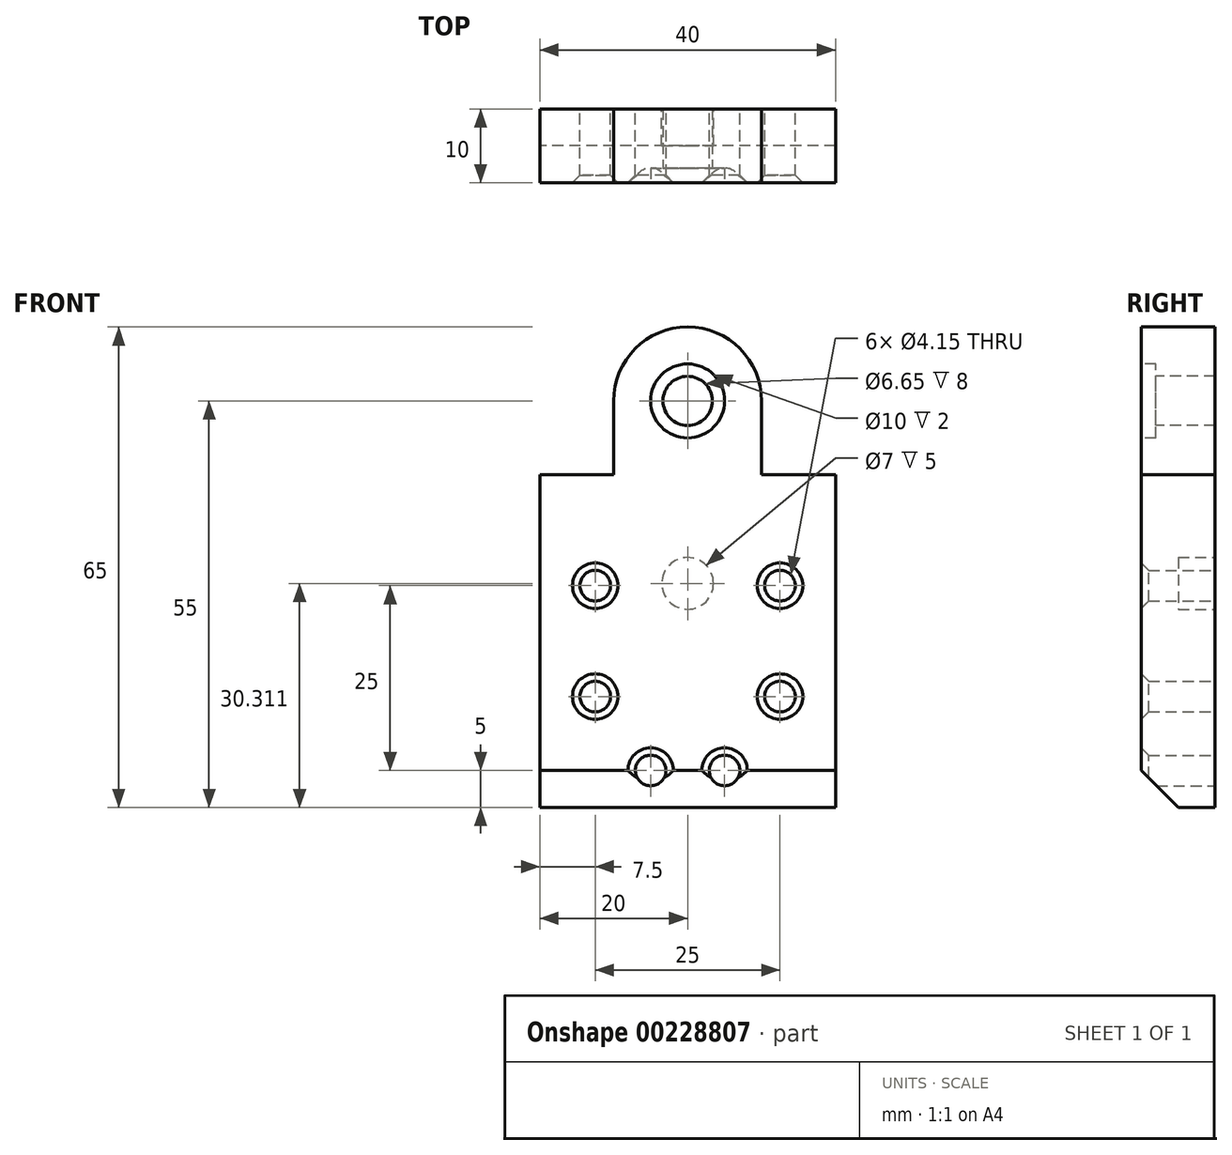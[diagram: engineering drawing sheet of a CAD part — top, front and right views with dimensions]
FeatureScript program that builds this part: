
annotation { "Feature Type Name" : "Feature", "Feature Type Description" : "" }
export const myFeature = defineFeature(function(context is Context, id is Id, definition is map)
    precondition{}
    {
        {
            var Q0;
            Q0=qCreatedBy(makeId("Front.planeOp"),FACE);
            var sketch = newSketch(context, id + "F0", { "sketchPlane" : qUnion([Q0])});
            skLineSegment(sketch, "E0.bottom", {"start": v(-20, 20) * mm, "end": v(20, 20) * mm});
            skLineSegment(sketch, "E0.top", {"start": v(-20, -20) * mm, "end": v(20, -20) * mm});
            skLineSegment(sketch, "E0.left", {"start": v(-20, 20) * mm, "end": v(-20, -20) * mm});
            skLineSegment(sketch, "E0.right", {"start": v(20, 20) * mm, "end": v(20, -20) * mm});
            skCircle(sketch, "E1", {"center": v(-5, -15) * mm, "radius": 2.07 * mm});
            skCircle(sketch, "E2.MirrorC", {"center": v(5, -15) * mm, "radius": 2.07 * mm});
            skCircle(sketch, "E3", {"center": v(-12.5, 10) * mm, "radius": 2.07 * mm});
            skCircle(sketch, "E4.MirrorC", {"center": v(12.5, 10) * mm, "radius": 2.07 * mm});
            skLineSegment(sketch, "E5", {"start": v(-20, 2.5) * mm, "end": v(0, 2.5) * mm, "construction": true});
            skCircle(sketch, "E6.MirrorC", {"center": v(-12.5, -5) * mm, "radius": 2.07 * mm});
            skCircle(sketch, "E7.MirrorC", {"center": v(12.5, -5) * mm, "radius": 2.07 * mm});
            skSolve(sketch);
        }
        {
            var Q0;
            Q0=makeQuery(id+"F0.imprint","IMPRINT",FACE,{"disambiguationData":[TD([[makeQuery(id+"F0.imprint","IMPRINT",EDGE,{"derivedFrom":sQuery(id+"F0.wireOp",EDGE,"E0.bottom")}),-1.0]])]});
            extrude(context, id + "F1", {"entities" : qUnion([Q0]), "depth" : 10 * mm});
        }
        {
            var Q0;
            Q0=makeQuery(id+"F1.opExtrude","CAP_FACE",FACE,{"disambiguationData":[OSD([sQuery(id+"F0.wireOp",EDGE,"E0.bottom"),sQuery(id+"F0.wireOp",EDGE,"E0.top"),sQuery(id+"F0.wireOp",EDGE,"E0.left"),sQuery(id+"F0.wireOp",EDGE,"E0.right"),sQuery(id+"F0.wireOp",EDGE,"E1"),sQuery(id+"F0.wireOp",EDGE,"E2.MirrorC"),sQuery(id+"F0.wireOp",EDGE,"E3"),sQuery(id+"F0.wireOp",EDGE,"E4.MirrorC")])],"isStart":false});
            var sketch = newSketch(context, id + "F2", { "sketchPlane" : qUnion([Q0])});
            skArc(sketch, "E8", {"start": v(10, 35) * mm, "mid": v(0, 45) * mm, "end": v(-10, 35) * mm});
            skLineSegment(sketch, "E9", {"start": v(-10, 35) * mm, "end": v(-10, 20) * mm});
            skLineSegment(sketch, "E10", {"start": v(10, 35) * mm, "end": v(10, 20) * mm});
            skLineSegment(sketch, "E11.bottom", {"start": v(-20, 25) * mm, "end": v(-10, 25) * mm});
            skLineSegment(sketch, "E11.top", {"start": v(-20, 20) * mm, "end": v(-10, 20) * mm});
            skLineSegment(sketch, "E11.left", {"start": v(-20, 25) * mm, "end": v(-20, 20) * mm});
            skLineSegment(sketch, "E11.right", {"start": v(-10, 25) * mm, "end": v(-10, 20) * mm});
            skLineSegment(sketch, "E12.bottom", {"start": v(20, 25) * mm, "end": v(10, 25) * mm});
            skLineSegment(sketch, "E12.top", {"start": v(20, 20) * mm, "end": v(10, 20) * mm});
            skLineSegment(sketch, "E12.left", {"start": v(20, 25) * mm, "end": v(20, 20) * mm});
            skLineSegment(sketch, "E12.right", {"start": v(10, 25) * mm, "end": v(10, 20) * mm});
            skSolve(sketch);
        }
        {
            var Q0;
            Q0=makeQuery(id+"F2.imprint","IMPRINT",FACE,{"disambiguationData":[TD([[makeQuery(id+"F2.imprint","IMPRINT",EDGE,{"derivedFrom":sQuery(id+"F2.wireOp",EDGE,"E8")}),1.0]])]});
            var Q1;
            Q1=makeQuery(id+"F2.imprint","IMPRINT",FACE,{"disambiguationData":[TD([[makeQuery(id+"F2.imprint","IMPRINT",EDGE,{"derivedFrom":sQuery(id+"F2.wireOp",EDGE,"E11.bottom")}),-1.0]])]});
            var Q2;
            Q2=makeQuery(id+"F2.imprint","IMPRINT",FACE,{"disambiguationData":[TD([[makeQuery(id+"F2.imprint","IMPRINT",EDGE,{"derivedFrom":sQuery(id+"F2.wireOp",EDGE,"E12.bottom")}),1.0]])]});
            var Q3;
            Q3=makeQuery(id+"F1.opExtrude","CAP_FACE",FACE,{"disambiguationData":[OSD([sQuery(id+"F0.wireOp",EDGE,"E0.bottom"),sQuery(id+"F0.wireOp",EDGE,"E0.top"),sQuery(id+"F0.wireOp",EDGE,"E0.left"),sQuery(id+"F0.wireOp",EDGE,"E0.right"),sQuery(id+"F0.wireOp",EDGE,"E1"),sQuery(id+"F0.wireOp",EDGE,"E2.MirrorC"),sQuery(id+"F0.wireOp",EDGE,"E3"),sQuery(id+"F0.wireOp",EDGE,"E4.MirrorC")])],"isStart":true});
            extrude(context, id + "F3", {"entities" : qUnion([Q0, Q1, Q2]), "operationType" : NewBodyOperationType.ADD, "endBound" : BoundingType.UP_TO_SURFACE, "oppositeDirection" : true, "endBoundEntityFace" : qUnion([Q3]), "depth" : 25 * mm});
        }
        {
            var Q0;
            Q0=makeQuery(id+"F1.opExtrude","CAP_EDGE",EDGE,{"disambiguationData":[OSD([sQuery(id+"F0.wireOp",EDGE,"E1")])],"isStart":false});
            var Q1;
            Q1=makeQuery(id+"F1.opExtrude","CAP_EDGE",EDGE,{"disambiguationData":[OSD([sQuery(id+"F0.wireOp",EDGE,"E2.MirrorC")])],"isStart":false});
            var Q2;
            Q2=makeQuery(id+"F1.opExtrude","CAP_EDGE",EDGE,{"disambiguationData":[OSD([sQuery(id+"F0.wireOp",EDGE,"E3")])],"isStart":false});
            var Q3;
            Q3=makeQuery(id+"F1.opExtrude","CAP_EDGE",EDGE,{"disambiguationData":[OSD([sQuery(id+"F0.wireOp",EDGE,"E6.MirrorC")])],"isStart":false});
            var Q4;
            Q4=makeQuery(id+"F1.opExtrude","CAP_EDGE",EDGE,{"disambiguationData":[OSD([sQuery(id+"F0.wireOp",EDGE,"E7.MirrorC")])],"isStart":false});
            var Q5;
            Q5=makeQuery(id+"F1.opExtrude","CAP_EDGE",EDGE,{"disambiguationData":[OSD([sQuery(id+"F0.wireOp",EDGE,"E4.MirrorC")])],"isStart":false});
            chamfer(context, id + "F4", {"entities" : qUnion([Q0, Q1, Q2, Q3, Q4, Q5]), "width" : 1 * mm, "tangentPropagation" : true});
        }
        {
            var Q0;
            {var subQ0=sQuery(id+"F0.wireOp",EDGE,"E0.bottom");Q0=makeQuery(id+"F3.boolean.opBoolean","MERGE",FACE,{"derivedFrom":[makeQuery(id+"F1.opExtrude","CAP_FACE",FACE,{"disambiguationData":[OSD([subQ0,sQuery(id+"F0.wireOp",EDGE,"E0.top"),sQuery(id+"F0.wireOp",EDGE,"E0.left"),sQuery(id+"F0.wireOp",EDGE,"E0.right"),sQuery(id+"F0.wireOp",EDGE,"E1"),sQuery(id+"F0.wireOp",EDGE,"E2.MirrorC"),sQuery(id+"F0.wireOp",EDGE,"E3"),sQuery(id+"F0.wireOp",EDGE,"E4.MirrorC"),sQuery(id+"F0.wireOp",EDGE,"E6.MirrorC"),sQuery(id+"F0.wireOp",EDGE,"E7.MirrorC")])],"isStart":false}),makeQuery(id+"F3.opExtrude","CAP_FACE",FACE,{"disambiguationData":[OSD([subQ0,sQuery(id+"F2.wireOp",EDGE,"E8"),sQuery(id+"F2.wireOp",EDGE,"E9"),sQuery(id+"F2.wireOp",EDGE,"E10"),sQuery(id+"F2.wireOp",EDGE,"E11.bottom"),sQuery(id+"F2.wireOp",EDGE,"E11.top"),sQuery(id+"F2.wireOp",EDGE,"E11.left"),sQuery(id+"F2.wireOp",EDGE,"E12.bottom"),sQuery(id+"F2.wireOp",EDGE,"E12.top"),sQuery(id+"F2.wireOp",EDGE,"E12.left")])],"isStart":true})]});}
            var sketch = newSketch(context, id + "F5", { "sketchPlane" : qUnion([Q0])});
            skCircle(sketch, "E13", {"center": v(0, 35) * mm, "radius": 3.32 * mm});
            skSolve(sketch);
        }
        {
            var Q0;
            Q0=makeQuery(id+"F5.imprint","IMPRINT",FACE,{"disambiguationData":[TD([[makeQuery(id+"F5.imprint","IMPRINT",EDGE,{"derivedFrom":sQuery(id+"F5.wireOp",EDGE,"E13")}),1.0]])]});
            extrude(context, id + "F6", {"entities" : qUnion([Q0]), "operationType" : NewBodyOperationType.REMOVE, "endBound" : BoundingType.THROUGH_ALL, "oppositeDirection" : true, "depth" : 25 * mm});
        }
        {
            var Q0;
            {var subQ0=sQuery(id+"F0.wireOp",EDGE,"E0.bottom");Q0=makeQuery(id+"F3.boolean.opBoolean","MERGE",FACE,{"derivedFrom":[makeQuery(id+"F1.opExtrude","CAP_FACE",FACE,{"disambiguationData":[OSD([subQ0,sQuery(id+"F0.wireOp",EDGE,"E0.top"),sQuery(id+"F0.wireOp",EDGE,"E0.left"),sQuery(id+"F0.wireOp",EDGE,"E0.right"),sQuery(id+"F0.wireOp",EDGE,"E1"),sQuery(id+"F0.wireOp",EDGE,"E2.MirrorC"),sQuery(id+"F0.wireOp",EDGE,"E3"),sQuery(id+"F0.wireOp",EDGE,"E4.MirrorC"),sQuery(id+"F0.wireOp",EDGE,"E6.MirrorC"),sQuery(id+"F0.wireOp",EDGE,"E7.MirrorC")])],"isStart":false}),makeQuery(id+"F3.opExtrude","CAP_FACE",FACE,{"disambiguationData":[OSD([subQ0,sQuery(id+"F2.wireOp",EDGE,"E8"),sQuery(id+"F2.wireOp",EDGE,"E9"),sQuery(id+"F2.wireOp",EDGE,"E10"),sQuery(id+"F2.wireOp",EDGE,"E11.bottom"),sQuery(id+"F2.wireOp",EDGE,"E11.top"),sQuery(id+"F2.wireOp",EDGE,"E11.left"),sQuery(id+"F2.wireOp",EDGE,"E12.bottom"),sQuery(id+"F2.wireOp",EDGE,"E12.top"),sQuery(id+"F2.wireOp",EDGE,"E12.left")])],"isStart":true})]});}
            var sketch = newSketch(context, id + "F7", { "sketchPlane" : qUnion([Q0])});
            skCircle(sketch, "E14", {"center": v(0, 35) * mm, "radius": 5 * mm});
            skSolve(sketch);
        }
        {
            var Q0;
            Q0=makeQuery(id+"F7.imprint","IMPRINT",FACE,{"disambiguationData":[TD([[makeQuery(id+"F7.imprint","IMPRINT",EDGE,{"derivedFrom":sQuery(id+"F7.wireOp",EDGE,"E14")}),1.0]])]});
            extrude(context, id + "F8", {"entities" : qUnion([Q0]), "operationType" : NewBodyOperationType.REMOVE, "oppositeDirection" : true, "depth" : 2 * mm});
        }
        {
            var Q0;
            {var subQ0=sQuery(id+"F0.wireOp",EDGE,"E0.bottom");Q0=makeQuery(id+"F3.boolean.opBoolean","MERGE",FACE,{"derivedFrom":[makeQuery(id+"F1.opExtrude","CAP_FACE",FACE,{"disambiguationData":[OSD([subQ0,sQuery(id+"F0.wireOp",EDGE,"E0.top"),sQuery(id+"F0.wireOp",EDGE,"E0.left"),sQuery(id+"F0.wireOp",EDGE,"E0.right"),sQuery(id+"F0.wireOp",EDGE,"E1"),sQuery(id+"F0.wireOp",EDGE,"E2.MirrorC"),sQuery(id+"F0.wireOp",EDGE,"E3"),sQuery(id+"F0.wireOp",EDGE,"E4.MirrorC"),sQuery(id+"F0.wireOp",EDGE,"E6.MirrorC"),sQuery(id+"F0.wireOp",EDGE,"E7.MirrorC")])],"isStart":false}),makeQuery(id+"F3.opExtrude","CAP_FACE",FACE,{"disambiguationData":[OSD([subQ0,sQuery(id+"F2.wireOp",EDGE,"E8"),sQuery(id+"F2.wireOp",EDGE,"E9"),sQuery(id+"F2.wireOp",EDGE,"E10"),sQuery(id+"F2.wireOp",EDGE,"E11.bottom"),sQuery(id+"F2.wireOp",EDGE,"E11.top"),sQuery(id+"F2.wireOp",EDGE,"E11.left"),sQuery(id+"F2.wireOp",EDGE,"E12.bottom"),sQuery(id+"F2.wireOp",EDGE,"E12.top"),sQuery(id+"F2.wireOp",EDGE,"E12.left")])],"isStart":true})]});}
            var Q1;
            {var subQ0=sQuery(id+"F0.wireOp",EDGE,"E7.MirrorC");var subQ1=sQuery(id+"F0.wireOp",EDGE,"E6.MirrorC");var subQ2=sQuery(id+"F0.wireOp",EDGE,"E4.MirrorC");var subQ3=sQuery(id+"F0.wireOp",EDGE,"E3");var subQ4=sQuery(id+"F0.wireOp",EDGE,"E2.MirrorC");var subQ5=sQuery(id+"F0.wireOp",EDGE,"E1");var subQ6=sQuery(id+"F0.wireOp",EDGE,"E0.right");var subQ7=sQuery(id+"F0.wireOp",EDGE,"E0.left");var subQ8=sQuery(id+"F0.wireOp",EDGE,"E0.top");var subQ9=sQuery(id+"F0.wireOp",EDGE,"E0.bottom");Q1=makeQuery(id+"F3.boolean.opBoolean","MERGE",FACE,{"derivedFrom":[makeQuery(id+"F1.opExtrude","CAP_FACE",FACE,{"disambiguationData":[OSD([subQ9,subQ8,subQ7,subQ6,subQ5,subQ4,subQ3,subQ2,subQ1,subQ0])],"isStart":true}),makeQuery(id+"F3.opExtrude","CAP_FACE",FACE,{"disambiguationData":[OSD([subQ9,subQ8,subQ7,subQ6,subQ5,subQ4,subQ3,subQ2,subQ1,subQ0])],"isStart":false})]});}
            cPlane(context, id + "F9", {"entities" : qUnion([Q0, Q1]), "cplaneType" : CPlaneType.MID_PLANE, "offset" : 25 * mm, "width" : 150 * mm, "height" : 150 * mm});
        }
        {
            var Q0;
            {var subQ0=sQuery(id+"F0.wireOp",EDGE,"E7.MirrorC");var subQ1=sQuery(id+"F0.wireOp",EDGE,"E6.MirrorC");var subQ2=sQuery(id+"F0.wireOp",EDGE,"E4.MirrorC");var subQ3=sQuery(id+"F0.wireOp",EDGE,"E3");var subQ4=sQuery(id+"F0.wireOp",EDGE,"E2.MirrorC");var subQ5=sQuery(id+"F0.wireOp",EDGE,"E1");var subQ6=sQuery(id+"F0.wireOp",EDGE,"E0.right");var subQ7=sQuery(id+"F0.wireOp",EDGE,"E0.left");var subQ8=sQuery(id+"F0.wireOp",EDGE,"E0.top");var subQ9=sQuery(id+"F0.wireOp",EDGE,"E0.bottom");Q0=makeQuery(id+"F3.boolean.opBoolean","MERGE",FACE,{"derivedFrom":[makeQuery(id+"F1.opExtrude","CAP_FACE",FACE,{"disambiguationData":[OSD([subQ9,subQ8,subQ7,subQ6,subQ5,subQ4,subQ3,subQ2,subQ1,subQ0])],"isStart":true}),makeQuery(id+"F3.opExtrude","CAP_FACE",FACE,{"disambiguationData":[OSD([subQ9,subQ8,subQ7,subQ6,subQ5,subQ4,subQ3,subQ2,subQ1,subQ0])],"isStart":false})]});}
            var sketch = newSketch(context, id + "F10", { "sketchPlane" : qUnion([Q0])});
            skCircle(sketch, "E15", {"center": v(0, 10.31) * mm, "radius": 3.5 * mm});
            skSolve(sketch);
        }
        {
            var Q0;
            Q0=makeQuery(id+"F10.imprint","IMPRINT",FACE,{"disambiguationData":[TD([[makeQuery(id+"F10.imprint","IMPRINT",EDGE,{"derivedFrom":sQuery(id+"F10.wireOp",EDGE,"E15")}),1.0]])]});
            extrude(context, id + "F11", {"entities" : qUnion([Q0]), "operationType" : NewBodyOperationType.REMOVE, "oppositeDirection" : true, "depth" : 5 * mm});
        }
        {
            var Q0;
            Q0=makeQuery(id+"F1.opExtrude","CAP_EDGE",EDGE,{"disambiguationData":[OSD([sQuery(id+"F0.wireOp",EDGE,"E0.top")])],"isStart":false});
            chamfer(context, id + "F12", {"entities" : qUnion([Q0]), "width" : 5 * mm, "tangentPropagation" : true});
        }
    });
